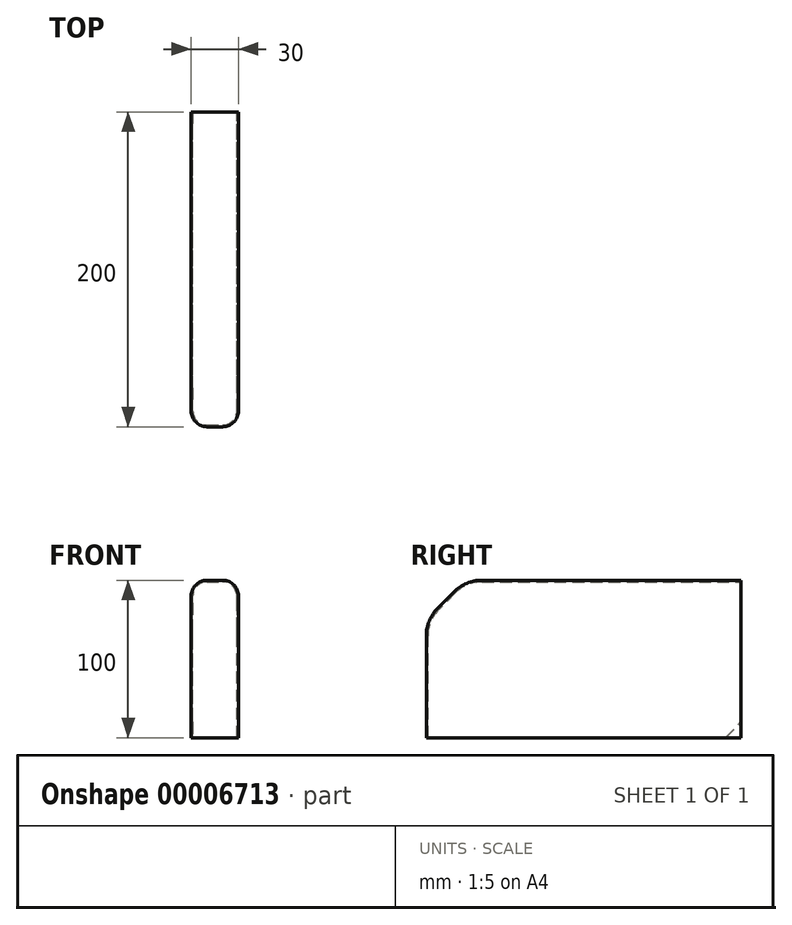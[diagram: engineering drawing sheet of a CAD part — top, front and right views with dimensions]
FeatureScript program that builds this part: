
annotation { "Feature Type Name" : "Feature", "Feature Type Description" : "" }
export const myFeature = defineFeature(function(context is Context, id is Id, definition is map)
    precondition{}
    {
        {
            var Q0;
            Q0=qCreatedBy(makeId("Front.planeOp"),FACE);
            var sketch = newSketch(context, id + "F0", { "sketchPlane" : qUnion([Q0])});
            skLineSegment(sketch, "E0.bottom", {"start": v(0, 0) * mm, "end": v(30, 0) * mm});
            skLineSegment(sketch, "E0.top", {"start": v(0, 100) * mm, "end": v(30, 100) * mm});
            skLineSegment(sketch, "E0.left", {"start": v(0, 0) * mm, "end": v(0, 100) * mm});
            skLineSegment(sketch, "E0.right", {"start": v(30, 0) * mm, "end": v(30, 100) * mm});
            skSolve(sketch);
        }
        {
            var Q0;
            Q0 = qSketchRegion(id + "F0", true);
            extrude(context, id + "F1", {"entities" : qUnion([Q0]), "endBound" : BoundingType.SYMMETRIC, "depth" : 200 * mm});
        }
        {
            var Q0;
            Q0=makeQuery(id+"F1.opExtrude","CAP_EDGE",EDGE,{"disambiguationData":[OSD([sQuery(id+"F0.wireOp",EDGE,"E0.top")])],"isStart":false});
            chamfer(context, id + "F7", {"entities" : qUnion([Q0]), "width" : 25 * mm, "tangentPropagation" : true});
        }
        {
            var Q0;
            {var subQ0=sQuery(id+"F0.wireOp",EDGE,"E0.top");Q0=makeQuery(id+"F7.opChamfer","BLEND_EDGE",EDGE,{"blendedFrom":[makeQuery(id+"F1.opExtrude","CAP_EDGE",EDGE,{"disambiguationData":[OSD([subQ0])],"isStart":false}),makeQuery(id+"F1.opExtrude","SWEPT_FACE",FACE,{"disambiguationData":[OSD([subQ0])]})],"blendedInto":[makeQuery(id+"F1.opExtrude","SWEPT_FACE",FACE,{"disambiguationData":[OSD([subQ0])]})]});}
            var Q1;
            {var subQ0=sQuery(id+"F0.wireOp",EDGE,"E0.top");Q1=makeQuery(id+"F7.opChamfer","BLEND_EDGE",EDGE,{"blendedFrom":[makeQuery(id+"F1.opExtrude","CAP_EDGE",EDGE,{"disambiguationData":[OSD([subQ0])],"isStart":false}),makeQuery(id+"F1.opExtrude","CAP_FACE",FACE,{"disambiguationData":[OSD([sQuery(id+"F0.wireOp",EDGE,"E0.bottom"),subQ0,sQuery(id+"F0.wireOp",EDGE,"E0.left"),sQuery(id+"F0.wireOp",EDGE,"E0.right")])],"isStart":false})],"blendedInto":[makeQuery(id+"F1.opExtrude","CAP_FACE",FACE,{"disambiguationData":[OSD([sQuery(id+"F0.wireOp",EDGE,"E0.bottom"),subQ0,sQuery(id+"F0.wireOp",EDGE,"E0.left"),sQuery(id+"F0.wireOp",EDGE,"E0.right")])],"isStart":false})]});}
            fillet(context, id + "F2", {"entities" : qUnion([Q0, Q1]), "radius" : 25 * mm, "tangentPropagation" : true, "allowEdgeOverflow" : false});
        }
        {
            var Q0;
            Q0=makeQuery(id+"F1.opExtrude","CAP_EDGE",EDGE,{"disambiguationData":[OSD([sQuery(id+"F0.wireOp",EDGE,"E0.right")])],"isStart":false});
            var Q1;
            Q1=makeQuery(id+"F1.opExtrude","CAP_EDGE",EDGE,{"disambiguationData":[OSD([sQuery(id+"F0.wireOp",EDGE,"E0.left")])],"isStart":false});
            fillet(context, id + "F3", {"entities" : qUnion([Q0, Q1]), "radius" : 10 * mm, "tangentPropagation" : true, "allowEdgeOverflow" : false});
        }
        {
            var Q0;
            Q0=makeQuery(id+"F1.opExtrude","SWEPT_FACE",FACE,{"disambiguationData":[OSD([sQuery(id+"F0.wireOp",EDGE,"E0.bottom")])]});
            var Q1;
            Q1=makeQuery(id+"F1.opExtrude","CAP_FACE",FACE,{"disambiguationData":[OSD([sQuery(id+"F0.wireOp",EDGE,"E0.bottom"),sQuery(id+"F0.wireOp",EDGE,"E0.top"),sQuery(id+"F0.wireOp",EDGE,"E0.left"),sQuery(id+"F0.wireOp",EDGE,"E0.right")])],"isStart":true});
            shell(context, id + "F8", {"entities" : qUnion([Q0, Q1]), "thickness" : 1 * mm});
        }
        {
            var Q0;
            Q0=makeQuery(id+"F1.opExtrude","SWEPT_FACE",FACE,{"disambiguationData":[OSD([sQuery(id+"F0.wireOp",EDGE,"E0.right")])]});
            var sketch = newSketch(context, id + "F4", { "sketchPlane" : qUnion([Q0])});
            skSolve(sketch);
        }
        {
            var Q0;
            Q0=makeQuery(id+"F1.opExtrude","CAP_EDGE",EDGE,{"disambiguationData":[OSD([sQuery(id+"F0.wireOp",EDGE,"E0.bottom")])],"isStart":true});
            chamfer(context, id + "F5", {"entities" : qUnion([Q0]), "width" : 10 * mm, "tangentPropagation" : true});
        }
    });
